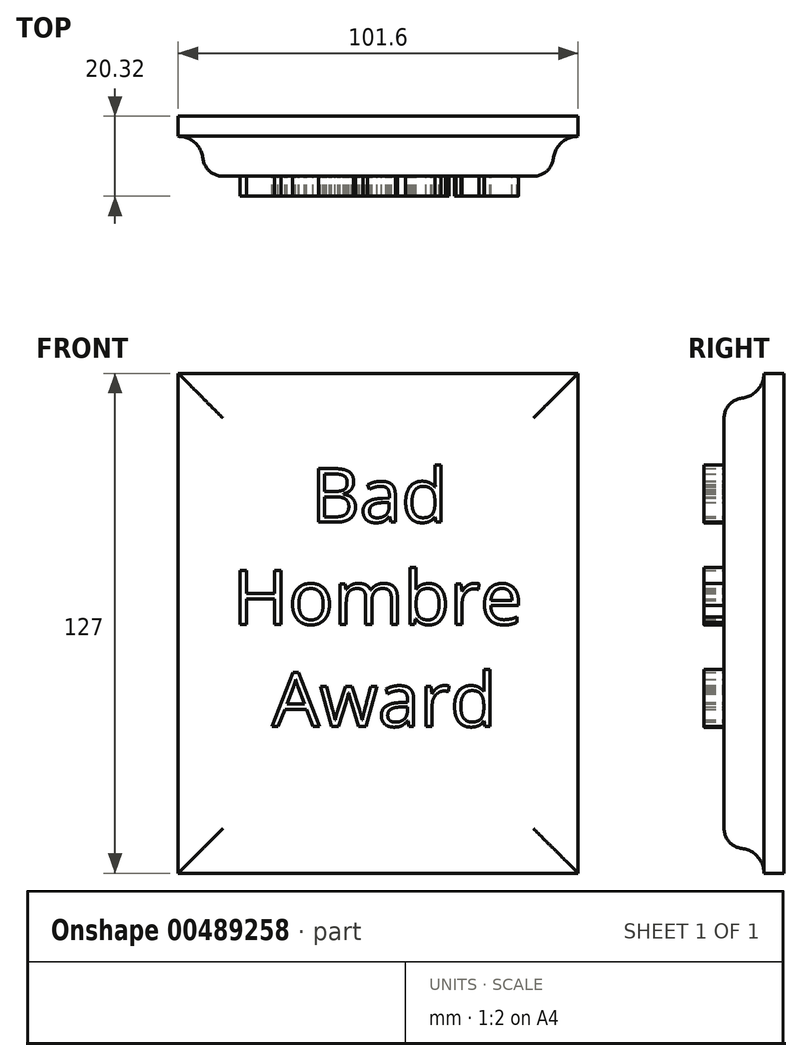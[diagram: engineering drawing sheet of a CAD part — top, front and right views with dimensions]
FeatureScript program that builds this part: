
annotation { "Feature Type Name" : "Feature", "Feature Type Description" : "" }
export const myFeature = defineFeature(function(context is Context, id is Id, definition is map)
    precondition{}
    {
        {
            var Q0;
            Q0=qCreatedBy(makeId("Front.planeOp"),FACE);
            var sketch = newSketch(context, id + "F0", { "sketchPlane" : qUnion([Q0])});
            skLineSegment(sketch, "E0.bottom", {"start": v(-101.6, 127) * mm, "end": v(0, 127) * mm});
            skLineSegment(sketch, "E0.top", {"start": v(-101.6, 0) * mm, "end": v(0, 0) * mm});
            skLineSegment(sketch, "E0.left", {"start": v(-101.6, 127) * mm, "end": v(-101.6, 0) * mm});
            skLineSegment(sketch, "E0.right", {"start": v(0, 127) * mm, "end": v(0, 0) * mm});
            skSolve(sketch);
        }
        {
            var Q0;
            Q0=qSketchRegion(id+"F0",true);
            extrude(context, id + "F1", {"entities" : qUnion([Q0]), "depth" : 15.24 * mm});
        }
        {
            var Q0;
            Q0=makeQuery(id+"F1.opExtrude","CAP_FACE",FACE,{"disambiguationData":[OSD([sQuery(id+"F0.wireOp",EDGE,"E0.bottom"),sQuery(id+"F0.wireOp",EDGE,"E0.top"),sQuery(id+"F0.wireOp",EDGE,"E0.left"),sQuery(id+"F0.wireOp",EDGE,"E0.right")])],"isStart":false});
            var sketch = newSketch(context, id + "F2", { "sketchPlane" : qUnion([Q0])});
            skLineSegment(sketch, "E1.bottom", {"start": v(-6.35, 6.35) * mm, "end": v(-95.25, 6.35) * mm});
            skLineSegment(sketch, "E1.top", {"start": v(-6.35, 120.65) * mm, "end": v(-95.25, 120.65) * mm});
            skLineSegment(sketch, "E1.left", {"start": v(-6.35, 6.35) * mm, "end": v(-6.35, 120.65) * mm});
            skLineSegment(sketch, "E1.right", {"start": v(-95.25, 6.35) * mm, "end": v(-95.25, 120.65) * mm});
            skLineSegment(sketch, "E2.bottom", {"start": v(-101.6, 127) * mm, "end": v(0, 127) * mm});
            skLineSegment(sketch, "E2.top", {"start": v(-101.6, 0) * mm, "end": v(0, 0) * mm});
            skLineSegment(sketch, "E2.left", {"start": v(-101.6, 127) * mm, "end": v(-101.6, 0) * mm});
            skLineSegment(sketch, "E2.right", {"start": v(0, 127) * mm, "end": v(0, 0) * mm});
            skSolve(sketch);
        }
        {
            var Q0;
            Q0=qSketchRegion(id+"F2",true);
            extrude(context, id + "F3", {"entities" : qUnion([Q0]), "operationType" : NewBodyOperationType.REMOVE, "oppositeDirection" : true, "depth" : 10.16 * mm});
        }
        {
            var Q0;
            Q0=makeQuery(id+"F3.boolean.opBoolean","COPY",EDGE,{"derivedFrom":makeQuery(id+"F3.opExtrude","CAP_EDGE",EDGE,{"disambiguationData":[OSD([sQuery(id+"F2.wireOp",EDGE,"E1.top")])],"isStart":false})});
            var Q1;
            Q1=makeQuery(id+"F3.boolean.opBoolean","COPY",EDGE,{"derivedFrom":makeQuery(id+"F3.opExtrude","CAP_EDGE",EDGE,{"disambiguationData":[OSD([sQuery(id+"F2.wireOp",EDGE,"E1.left")])],"isStart":false})});
            var Q2;
            Q2=makeQuery(id+"F3.boolean.opBoolean","COPY",EDGE,{"derivedFrom":makeQuery(id+"F3.opExtrude","CAP_EDGE",EDGE,{"disambiguationData":[OSD([sQuery(id+"F2.wireOp",EDGE,"E1.right")])],"isStart":false})});
            var Q3;
            Q3=makeQuery(id+"F3.boolean.opBoolean","COPY",EDGE,{"derivedFrom":makeQuery(id+"F3.opExtrude","CAP_EDGE",EDGE,{"disambiguationData":[OSD([sQuery(id+"F2.wireOp",EDGE,"E1.bottom")])],"isStart":false})});
            fillet(context, id + "F4", {"entities" : qUnion([Q0, Q1, Q2, Q3]), "radius" : 6.35 * mm, "tangentPropagation" : true, "allowEdgeOverflow" : false});
        }
        {
            var Q0;
            Q0=makeQuery(id+"F1.opExtrude","CAP_FACE",FACE,{"disambiguationData":[OSD([sQuery(id+"F0.wireOp",EDGE,"E0.bottom"),sQuery(id+"F0.wireOp",EDGE,"E0.top"),sQuery(id+"F0.wireOp",EDGE,"E0.left"),sQuery(id+"F0.wireOp",EDGE,"E0.right")])],"isStart":false});
            fillet(context, id + "F5", {"entities" : qUnion([Q0]), "radius" : 5.08 * mm, "tangentPropagation" : true, "allowEdgeOverflow" : false});
        }
        {
            var Q0;
            Q0=makeQuery(id+"F1.opExtrude","CAP_FACE",FACE,{"disambiguationData":[OSD([sQuery(id+"F0.wireOp",EDGE,"E0.bottom"),sQuery(id+"F0.wireOp",EDGE,"E0.top"),sQuery(id+"F0.wireOp",EDGE,"E0.left"),sQuery(id+"F0.wireOp",EDGE,"E0.right")])],"isStart":false});
            var sketch = newSketch(context, id + "F6", { "sketchPlane" : qUnion([Q0])});
            skText(sketch, "E3", { "text": "    Bad\nHombre\n  Award", "fontName": "OpenSans-Regular.ttf"});
            const initialGuessF6  = {"E3": [-0.0877, 0.0892, 1, 0, 0.01374]};
            skSetInitialGuess(sketch, initialGuessF6);
            skSolve(sketch);
        }
        {
            var Q0;
            Q0=qSketchRegion(id+"F6",true);
            extrude(context, id + "F7", {"entities" : qUnion([Q0]), "operationType" : NewBodyOperationType.ADD, "depth" : 5.08 * mm});
        }
    });
